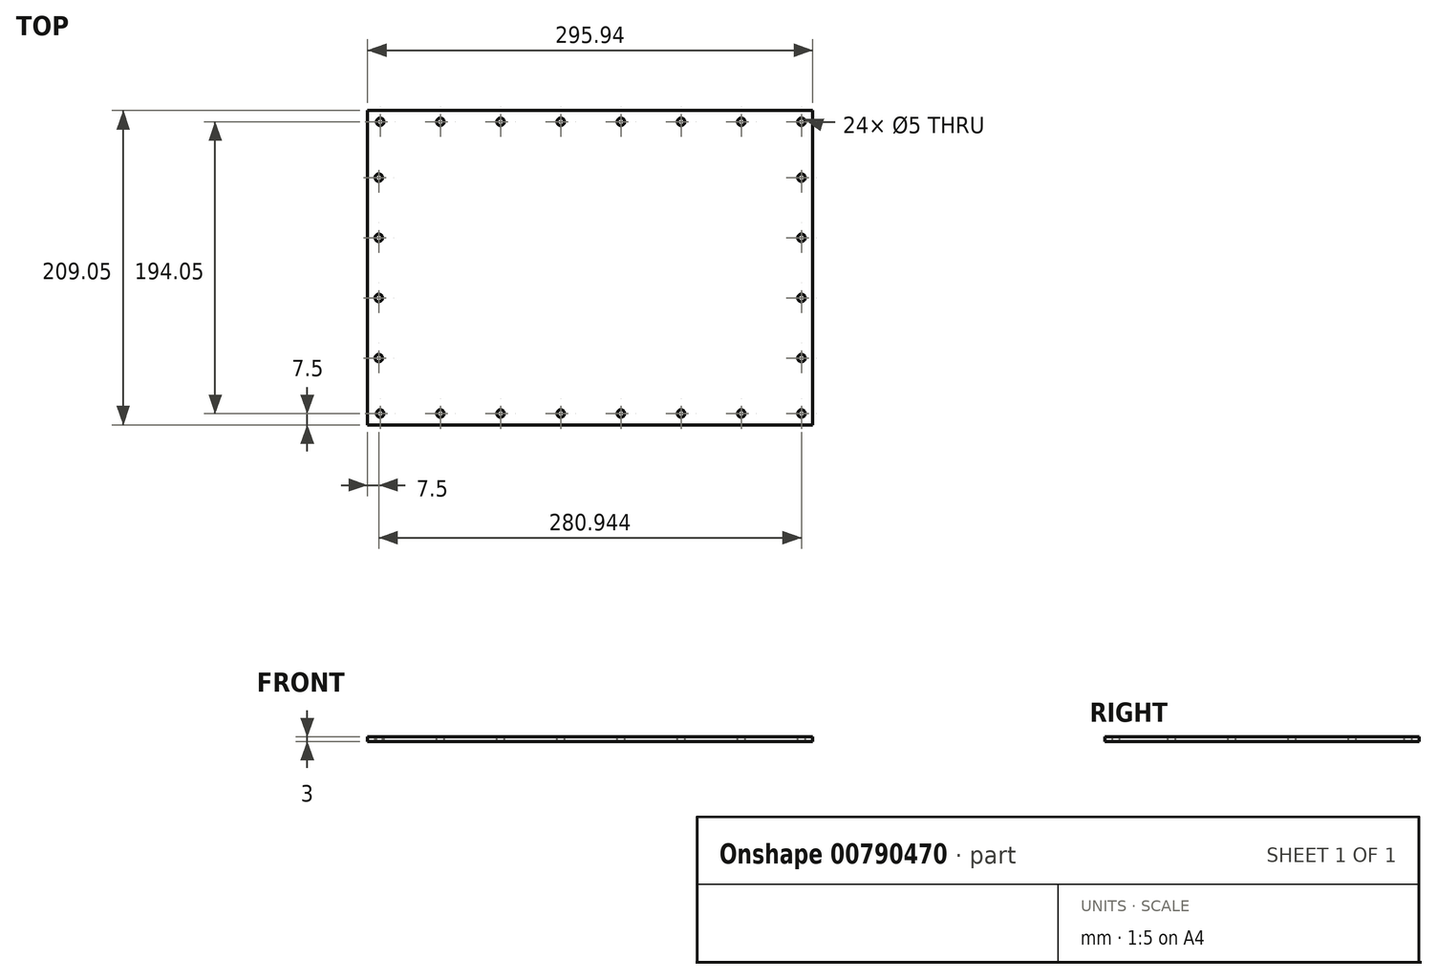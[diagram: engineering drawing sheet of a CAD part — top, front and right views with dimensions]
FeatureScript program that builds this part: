
annotation { "Feature Type Name" : "Feature", "Feature Type Description" : "" }
export const myFeature = defineFeature(function(context is Context, id is Id, definition is map)
    precondition{}
    {
        {
            var Q0;
            Q0=qCreatedBy(makeId("Front.planeOp"),FACE);
            var sketch = newSketch(context, id + "F0", { "sketchPlane" : qUnion([Q0])});
            skLineSegment(sketch, "E0.bottom", {"start": v(0, 0) * mm, "end": v(295.94, 0) * mm});
            skLineSegment(sketch, "E0.top", {"start": v(0, 3) * mm, "end": v(295.94, 3) * mm});
            skLineSegment(sketch, "E0.left", {"start": v(0, 0) * mm, "end": v(0, 3) * mm});
            skLineSegment(sketch, "E0.right", {"start": v(295.94, 0) * mm, "end": v(295.94, 3) * mm});
            skSolve(sketch);
        }
        {
            var Q0;
            Q0=makeQuery(id+"F0.imprint","IMPRINT",FACE,{"disambiguationData":[TD([[makeQuery(id+"F0.imprint","IMPRINT",EDGE,{"derivedFrom":sQuery(id+"F0.wireOp",EDGE,"E0.bottom")}),1.0]])]});
            extrude(context, id + "F1", {"entities" : qUnion([Q0]), "depth" : (158.25 + 50.8) * mm, "offsetDistance" : 25 * mm});
        }
        {
            var Q0;
            Q0=makeQuery(id+"F1.opExtrude","SWEPT_FACE",FACE,{"disambiguationData":[OSD([sQuery(id+"F0.wireOp",EDGE,"E0.top")])]});
            var sketch = newSketch(context, id + "F2", { "sketchPlane" : qUnion([Q0])});
            skLineSegment(sketch, "E1", {"start": v(25.4, -25.4) * mm, "end": v(25.4, -183.65) * mm, "construction": true});
            skLineSegment(sketch, "E2", {"start": v(25.4, -183.65) * mm, "end": v(270.54, -183.65) * mm, "construction": true});
            skLineSegment(sketch, "E3", {"start": v(270.54, -183.65) * mm, "end": v(270.54, -25.4) * mm, "construction": true});
            skLineSegment(sketch, "E4", {"start": v(270.54, -25.4) * mm, "end": v(25.4, -25.4) * mm, "construction": true});
            skLineSegment(sketch, "E5", {"start": v(25.4, 10.2) * mm, "end": v(0, 10.2) * mm, "construction": true});
            skLineSegment(sketch, "E6", {"start": v(308.08, -25.4) * mm, "end": v(308.08, 0) * mm, "construction": true});
            skLineSegment(sketch, "E7", {"start": v(304.56, -183.65) * mm, "end": v(304.56, -209.05) * mm, "construction": true});
            skLineSegment(sketch, "E8", {"start": v(270.54, 18.55) * mm, "end": v(295.94, 18.55) * mm, "construction": true});
            skLineSegment(sketch, "E9.0", {"start": v(7.5, -7.5) * mm, "end": v(7.5, -201.55) * mm, "construction": true});
            skLineSegment(sketch, "E9.1", {"start": v(288.44, -7.5) * mm, "end": v(7.5, -7.5) * mm, "construction": true});
            skLineSegment(sketch, "E9.2", {"start": v(288.44, -201.55) * mm, "end": v(288.44, -7.5) * mm, "construction": true});
            skLineSegment(sketch, "E9.3", {"start": v(7.5, -201.55) * mm, "end": v(288.44, -201.55) * mm, "construction": true});
            skLineSegment(sketch, "E10", {"start": v(25.4, -183.65) * mm, "end": v(0, -183.65) * mm, "construction": true});
            skLineSegment(sketch, "E11", {"start": v(25.4, -25.4) * mm, "end": v(0, -25.4) * mm, "construction": true});
            skLineSegment(sketch, "E12", {"start": v(270.54, -25.4) * mm, "end": v(295.94, -25.4) * mm, "construction": true});
            skLineSegment(sketch, "E13", {"start": v(270.54, -183.65) * mm, "end": v(295.94, -183.65) * mm, "construction": true});
            skLineSegment(sketch, "E14.0", {"start": v(278.44, -17.5) * mm, "end": v(17.5, -17.5) * mm, "construction": true});
            skLineSegment(sketch, "E14.1", {"start": v(278.44, -191.55) * mm, "end": v(278.44, -17.5) * mm, "construction": true});
            skLineSegment(sketch, "E14.2", {"start": v(17.5, -191.55) * mm, "end": v(278.44, -191.55) * mm, "construction": true});
            skLineSegment(sketch, "E14.3", {"start": v(17.5, -17.5) * mm, "end": v(17.5, -191.55) * mm, "construction": true});
            skCircle(sketch, "E15", {"center": v(288.44, -44.65) * mm, "radius": 2.5 * mm});
            skCircle(sketch, "E16", {"center": v(288.44, -84.65) * mm, "radius": 2.5 * mm});
            skCircle(sketch, "E17", {"center": v(288.44, -164.65) * mm, "radius": 2.5 * mm});
            skCircle(sketch, "E18", {"center": v(288.44, -124.65) * mm, "radius": 2.5 * mm});
            skCircle(sketch, "E19", {"center": v(288.44, -201.55) * mm, "radius": 2.5 * mm});
            skCircle(sketch, "E20", {"center": v(248.44, -201.55) * mm, "radius": 2.5 * mm});
            skCircle(sketch, "E21", {"center": v(208.44, -201.55) * mm, "radius": 2.5 * mm});
            skCircle(sketch, "E22", {"center": v(168.44, -201.55) * mm, "radius": 2.5 * mm});
            skCircle(sketch, "E23", {"center": v(128.44, -201.55) * mm, "radius": 2.5 * mm});
            skCircle(sketch, "E24", {"center": v(88.44, -201.55) * mm, "radius": 2.5 * mm});
            skCircle(sketch, "E25", {"center": v(48.44, -201.55) * mm, "radius": 2.5 * mm});
            skPoint(sketch, "E26", {"position": v(147.97, -201.55) * mm});
            skCircle(sketch, "E27", {"center": v(8.44, -201.55) * mm, "radius": 2.5 * mm});
            skLineSegment(sketch, "E28", {"start": v(147.97, 0) * mm, "end": v(147.97, -209.05) * mm, "construction": true});
            skLineSegment(sketch, "E29", {"start": v(0, -104.53) * mm, "end": v(295.94, -104.53) * mm, "construction": true});
            skCircle(sketch, "E30.MirrorC", {"center": v(7.5, -164.65) * mm, "radius": 2.5 * mm});
            skCircle(sketch, "E31.MirrorC", {"center": v(7.5, -124.65) * mm, "radius": 2.5 * mm});
            skCircle(sketch, "E32.MirrorC", {"center": v(7.5, -84.65) * mm, "radius": 2.5 * mm});
            skCircle(sketch, "E33.MirrorC", {"center": v(7.5, -44.65) * mm, "radius": 2.5 * mm});
            skCircle(sketch, "E34.MirrorC", {"center": v(8.44, -7.5) * mm, "radius": 2.5 * mm});
            skCircle(sketch, "E35.MirrorC", {"center": v(48.44, -7.5) * mm, "radius": 2.5 * mm});
            skCircle(sketch, "E36.MirrorC", {"center": v(88.44, -7.5) * mm, "radius": 2.5 * mm});
            skCircle(sketch, "E37.MirrorC", {"center": v(128.44, -7.5) * mm, "radius": 2.5 * mm});
            skCircle(sketch, "E38.MirrorC", {"center": v(168.44, -7.5) * mm, "radius": 2.5 * mm});
            skCircle(sketch, "E39.MirrorC", {"center": v(208.44, -7.5) * mm, "radius": 2.5 * mm});
            skCircle(sketch, "E40.MirrorC", {"center": v(248.44, -7.5) * mm, "radius": 2.5 * mm});
            skCircle(sketch, "E41.MirrorC", {"center": v(288.44, -7.5) * mm, "radius": 2.5 * mm});
            skSolve(sketch);
        }
        {
            var Q0;
            Q0 = qSketchRegion(id + "F2", true);
            extrude(context, id + "F3", {"entities" : qUnion([Q0]), "operationType" : NewBodyOperationType.REMOVE, "endBound" : BoundingType.UP_TO_NEXT, "oppositeDirection" : true, "depth" : 25 * mm, "offsetDistance" : 25 * mm});
        }
    });
